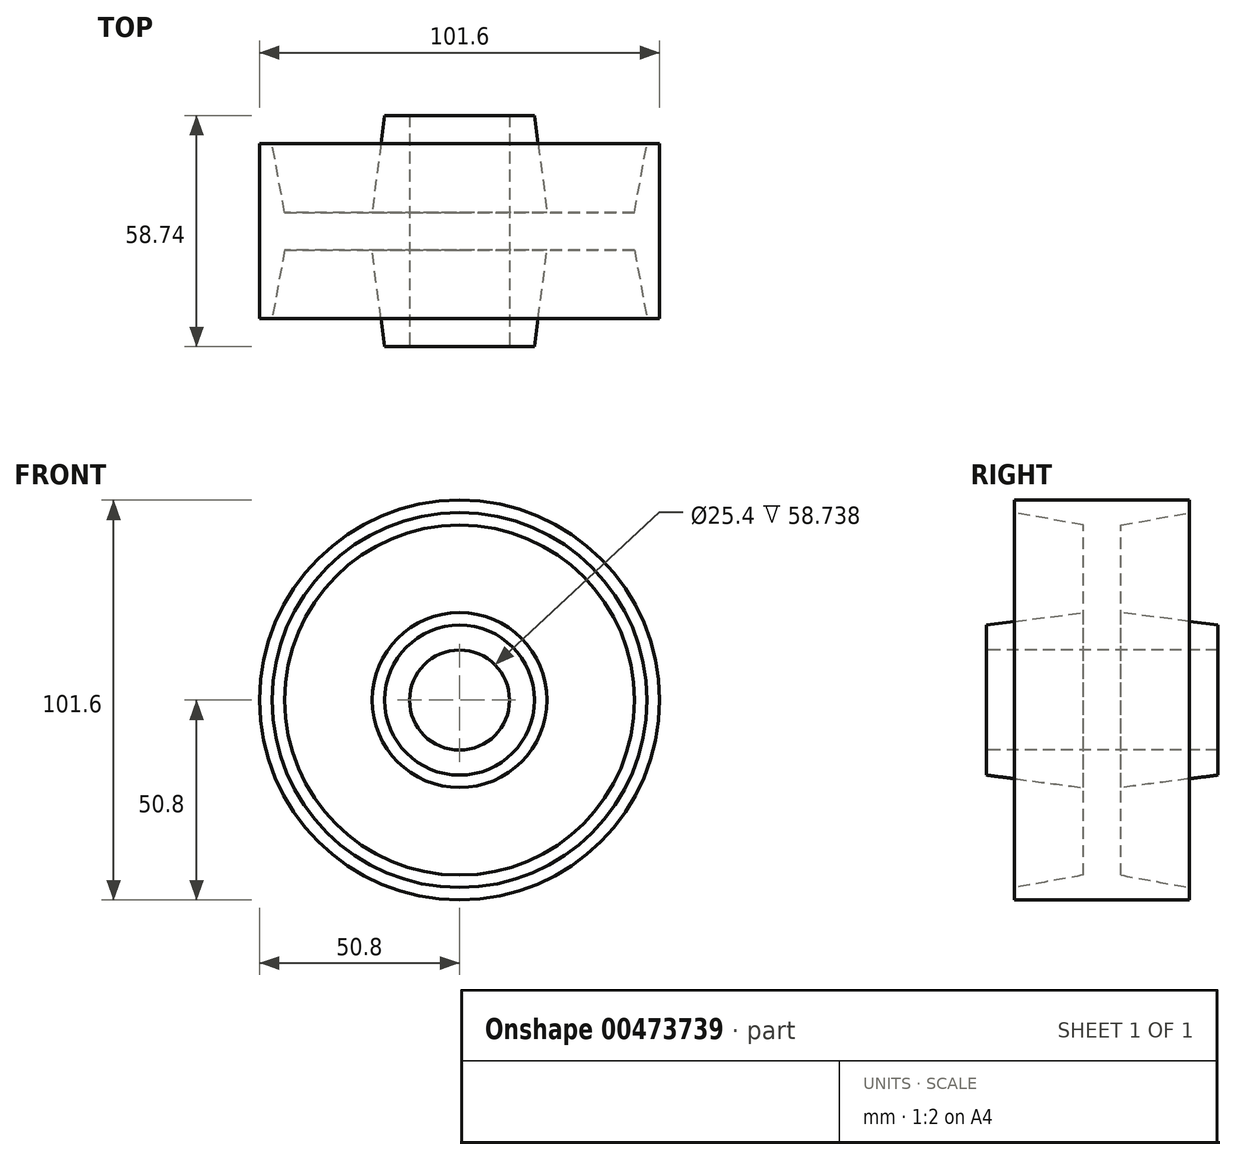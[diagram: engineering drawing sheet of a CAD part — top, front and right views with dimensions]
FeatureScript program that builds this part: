
annotation { "Feature Type Name" : "Feature", "Feature Type Description" : "" }
export const myFeature = defineFeature(function(context is Context, id is Id, definition is map)
    precondition{}
    {
        {
            var Q0;
            Q0=qCreatedBy(makeId("Right.planeOp"),FACE);
            var sketch = newSketch(context, id + "F0", { "sketchPlane" : qUnion([Q0])});
            skLineSegment(sketch, "E0", {"start": v(-69.48, 0) * mm, "end": v(77.6, 0) * mm});
            skLineSegment(sketch, "E1", {"start": v(-60.27, 12.7) * mm, "end": v(53.1, 12.7) * mm});
            skLineSegment(sketch, "E2", {"start": v(-60.27, 12.7) * mm, "end": v(-60.27, 19.05) * mm});
            skLineSegment(sketch, "E3", {"start": v(-60.27, 19.05) * mm, "end": v(-35.66, 22.22) * mm});
            skLineSegment(sketch, "E4", {"start": v(-35.66, 22.23) * mm, "end": v(-35.66, 44.45) * mm});
            skLineSegment(sketch, "E5", {"start": v(-26.14, 22.23) * mm, "end": v(-26.14, 44.45) * mm});
            skLineSegment(sketch, "E6", {"start": v(-53.13, 47.62) * mm, "end": v(-74.68, 47.62) * mm});
            skLineSegment(sketch, "E7", {"start": v(-53.13, 47.62) * mm, "end": v(-53.13, 50.8) * mm});
            skLineSegment(sketch, "E8", {"start": v(-35.66, 44.45) * mm, "end": v(-53.13, 47.62) * mm});
            skLineSegment(sketch, "E9", {"start": v(-53.13, 50.8) * mm, "end": v(-8.68, 50.8) * mm});
            skLineSegment(sketch, "E10", {"start": v(-8.68, 50.8) * mm, "end": v(-8.68, 47.62) * mm});
            skLineSegment(sketch, "E11", {"start": v(-8.68, 47.62) * mm, "end": v(-26.14, 44.45) * mm});
            skLineSegment(sketch, "E12", {"start": v(-26.14, 22.22) * mm, "end": v(-1.53, 19.05) * mm});
            skLineSegment(sketch, "E13", {"start": v(-1.53, 19.05) * mm, "end": v(-1.53, 12.7) * mm});
            skLineSegment(sketch, "E14", {"start": v(-30.9, 66.04) * mm, "end": v(-30.9, -18.21) * mm});
            skPoint(sketch, "E14.startSnap0", {"position": v(-30.9, 50.8) * mm});
            skSolve(sketch);
        }
        {
            var Q0;
            {var subQ5=sQuery(id+"F0.wireOp",EDGE,"E2");Q0=makeQuery(id+"F0.imprint","IMPRINT",FACE,{"disambiguationData":[TD([[makeQuery(id+"F0.imprint","IMPRINT",EDGE,{"derivedFrom":subQ5}),-1.0]])]});}
            var Q1;
            Q1=makeQuery(id+"F0.imprint","IMPRINT",FACE,{"disambiguationData":[TD([[makeQuery(id+"F0.imprint","IMPRINT",EDGE,{"derivedFrom":sQuery(id+"F0.wireOp",EDGE,"E5")}),1.0]])]});
            var Q2;
            Q2=sQuery(id+"F0.wireOp",EDGE,"E0");
            revolve(context, id + "F1", {"entities" : qUnion([Q0, Q1]), "axis" : qUnion([Q2]), "revolveType" : RevolveType.FULL});
        }
    });
